# Revit family: Faucet-Lavatory-KOHLER-Forte-K-10215-4
name_source: partatom
category: Plumbing Fixtures
revit_build: Autodesk Revit 2015 (Build: 20140606_1530(x64)
units: mm (PartAtom-declared; Revit-internal decimal feet)

## types (3) — shared parameters
ADA Compliant = Yes
Assembly Code = D2010900
CW Connection = Yes
Date Modified = 09/14/2017
Default Elevation = 36"
Description = Forte Single-handle bathroom sink faucet
Flow Rate = 1 GPM
HW Connection = Yes
Height = 8 9/16"
Inlet Connector = Inlet Connection
Length = 7 23/32"
Manufacturer = Kohler
MasterFormat 1995 = 15410
MasterFormat 2004 = 22.41.39
Material = Brass construction
Outlet Connector = Outlet Connection
Pressure = 60.00 psi
Product Documentation Link = http://www.us.kohler.com
Product Name = Forte
Product Page URL = http://www.us.kohler.com
Spout Reach = 5 1/8"
URL = http://www.us.kohler.com
Waste Connection = Yes
Width = 6 19/32"

## per-type parameters (varying)
| type | Finish | Model | Type |
| CP-Polished Chrome | Kohler-Metal-CP-Polished_Chrome | K-10215-4-CP | 1 |
| G-Brushed Chrome | Kohler-Metal-G-Brushed_Chrome | K-10215-4-G | 2 |
| BN-Vibrant Brushed Nickel | Kohler-Metal-BN-Vibrant_Brushed_Nickel | K-10215-4-BN | 3 |

## geometry (parser evidence)
native form markers: Sweep x5
no freeform markers — native parametric forms only
